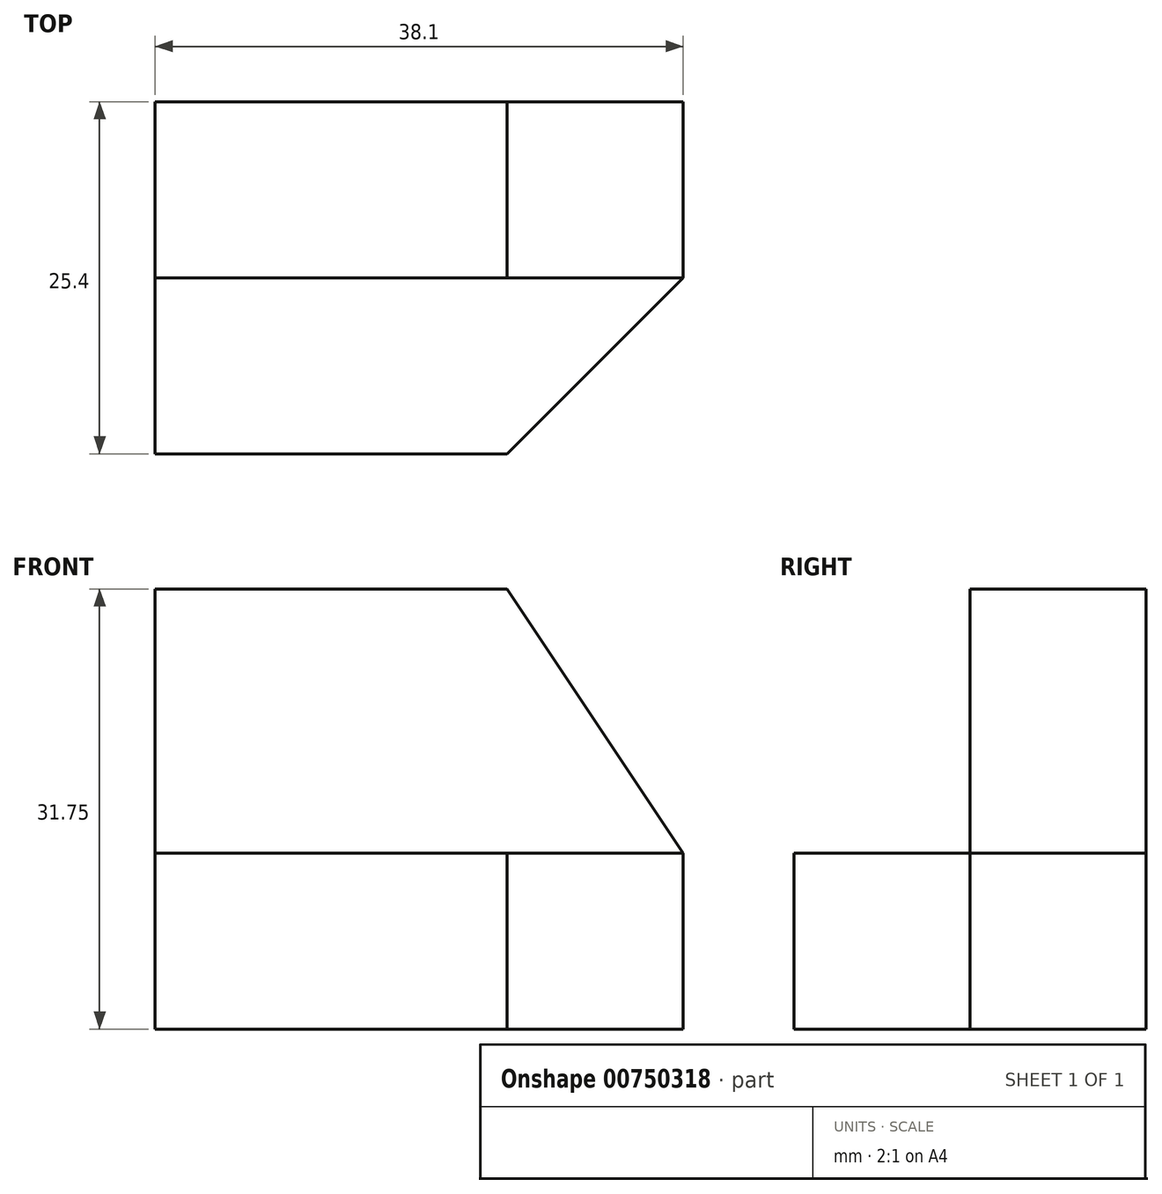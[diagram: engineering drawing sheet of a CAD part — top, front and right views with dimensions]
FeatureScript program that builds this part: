
annotation { "Feature Type Name" : "Feature", "Feature Type Description" : "" }
export const myFeature = defineFeature(function(context is Context, id is Id, definition is map)
    precondition{}
    {
        {
            var Q0;
            Q0=qCreatedBy(makeId("Front.planeOp"),FACE);
            var sketch = newSketch(context, id + "F0", { "sketchPlane" : qUnion([Q0])});
            skLineSegment(sketch, "E0", {"start": v(0, 0) * mm, "end": v(0, 31.75) * mm});
            skLineSegment(sketch, "E1", {"start": v(0, 31.75) * mm, "end": v(38.1, 31.75) * mm});
            skLineSegment(sketch, "E2", {"start": v(38.1, 31.75) * mm, "end": v(38.1, 0) * mm});
            skLineSegment(sketch, "E3", {"start": v(38.1, 0) * mm, "end": v(0, 0) * mm});
            skSolve(sketch);
        }
        {
            var Q0;
            Q0 = qSketchRegion(id + "F0", true);
            extrude(context, id + "F1", {"entities" : qUnion([Q0]), "depth" : 25.4 * mm, "offsetDistance" : 25.4 * mm});
        }
        {
            var Q0;
            Q0=makeQuery(id+"F1.opExtrude","SWEPT_FACE",FACE,{"disambiguationData":[OSD([sQuery(id+"F0.wireOp",EDGE,"E2")])]});
            var sketch = newSketch(context, id + "F2", { "sketchPlane" : qUnion([Q0])});
            skLineSegment(sketch, "E4", {"start": v(-12.7, 31.75) * mm, "end": v(-12.7, 12.7) * mm});
            skLineSegment(sketch, "E5", {"start": v(-12.7, 12.7) * mm, "end": v(-25.4, 12.7) * mm});
            skLineSegment(sketch, "E6", {"start": v(-25.4, 12.7) * mm, "end": v(-25.4, 31.75) * mm});
            skLineSegment(sketch, "E7", {"start": v(-25.4, 31.75) * mm, "end": v(-12.7, 31.75) * mm});
            skSolve(sketch);
        }
        {
            var Q0;
            Q0 = qSketchRegion(id + "F2", true);
            extrude(context, id + "F3", {"entities" : qUnion([Q0]), "operationType" : NewBodyOperationType.REMOVE, "oppositeDirection" : true, "depth" : 38.1 * mm, "offsetDistance" : 25.4 * mm});
        }
        {
            var Q0;
            Q0=makeQuery(id+"F3.boolean.opBoolean","COPY",FACE,{"derivedFrom":makeQuery(id+"F3.opExtrude","SWEPT_FACE",FACE,{"disambiguationData":[OSD([sQuery(id+"F2.wireOp",EDGE,"E5")])]})});
            var sketch = newSketch(context, id + "F4", { "sketchPlane" : qUnion([Q0])});
            skLineSegment(sketch, "E8", {"start": v(25.4, -25.4) * mm, "end": v(38.1, -12.7) * mm});
            skLineSegment(sketch, "E9", {"start": v(38.1, -12.7) * mm, "end": v(38.1, -25.4) * mm});
            skLineSegment(sketch, "E10", {"start": v(38.1, -25.4) * mm, "end": v(25.4, -25.4) * mm});
            skSolve(sketch);
        }
        {
            var Q0;
            Q0 = qSketchRegion(id + "F4", true);
            extrude(context, id + "F5", {"entities" : qUnion([Q0]), "operationType" : NewBodyOperationType.REMOVE, "oppositeDirection" : true, "depth" : 25.4 * mm, "offsetDistance" : 25.4 * mm});
        }
        {
            var Q0;
            Q0=makeQuery(id+"F3.boolean.opBoolean","COPY",FACE,{"derivedFrom":makeQuery(id+"F3.opExtrude","SWEPT_FACE",FACE,{"disambiguationData":[OSD([sQuery(id+"F2.wireOp",EDGE,"E4")])]})});
            var sketch = newSketch(context, id + "F6", { "sketchPlane" : qUnion([Q0])});
            skLineSegment(sketch, "E11", {"start": v(25.4, 31.75) * mm, "end": v(38.1, 12.7) * mm});
            skLineSegment(sketch, "E12", {"start": v(38.1, 12.7) * mm, "end": v(38.1, 31.75) * mm});
            skLineSegment(sketch, "E13", {"start": v(38.1, 31.75) * mm, "end": v(25.4, 31.75) * mm});
            skSolve(sketch);
        }
        {
            var Q0;
            Q0 = qSketchRegion(id + "F6", true);
            extrude(context, id + "F7", {"entities" : qUnion([Q0]), "operationType" : NewBodyOperationType.REMOVE, "oppositeDirection" : true, "depth" : 25.4 * mm, "offsetDistance" : 25.4 * mm});
        }
    });
